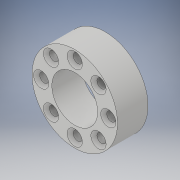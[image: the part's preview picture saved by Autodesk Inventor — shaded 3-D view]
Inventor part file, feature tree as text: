
AUTODESK INVENTOR PART (.ipt)
format: ipt  version: 2019 (Build 230136000, 136)  size: 176,640 bytes
history: native  units: mm
features: extrude x1, chamfer x1, sketch x1
ambient origin geometry x8: Origin, YZ Plane, XZ Plane, XY Plane, X Axis, Y Axis, Z Axis, Center Point
bodies: Solid1 (feature_tree)
feature tree (3):
  extrude  "Extrusion1"  Depth=2.0mm
  chamfer  "Chamfer1"  Distance=3.0mm
  sketch  "Sketch1"  dims[d0=28.0mm d1=15.0mm d2=3.0mm d3=80.0mm d5=360.0deg d7=10.0mm d8=0.0mm d10=1.0mm d11=2.0mm d12=45.0deg]
